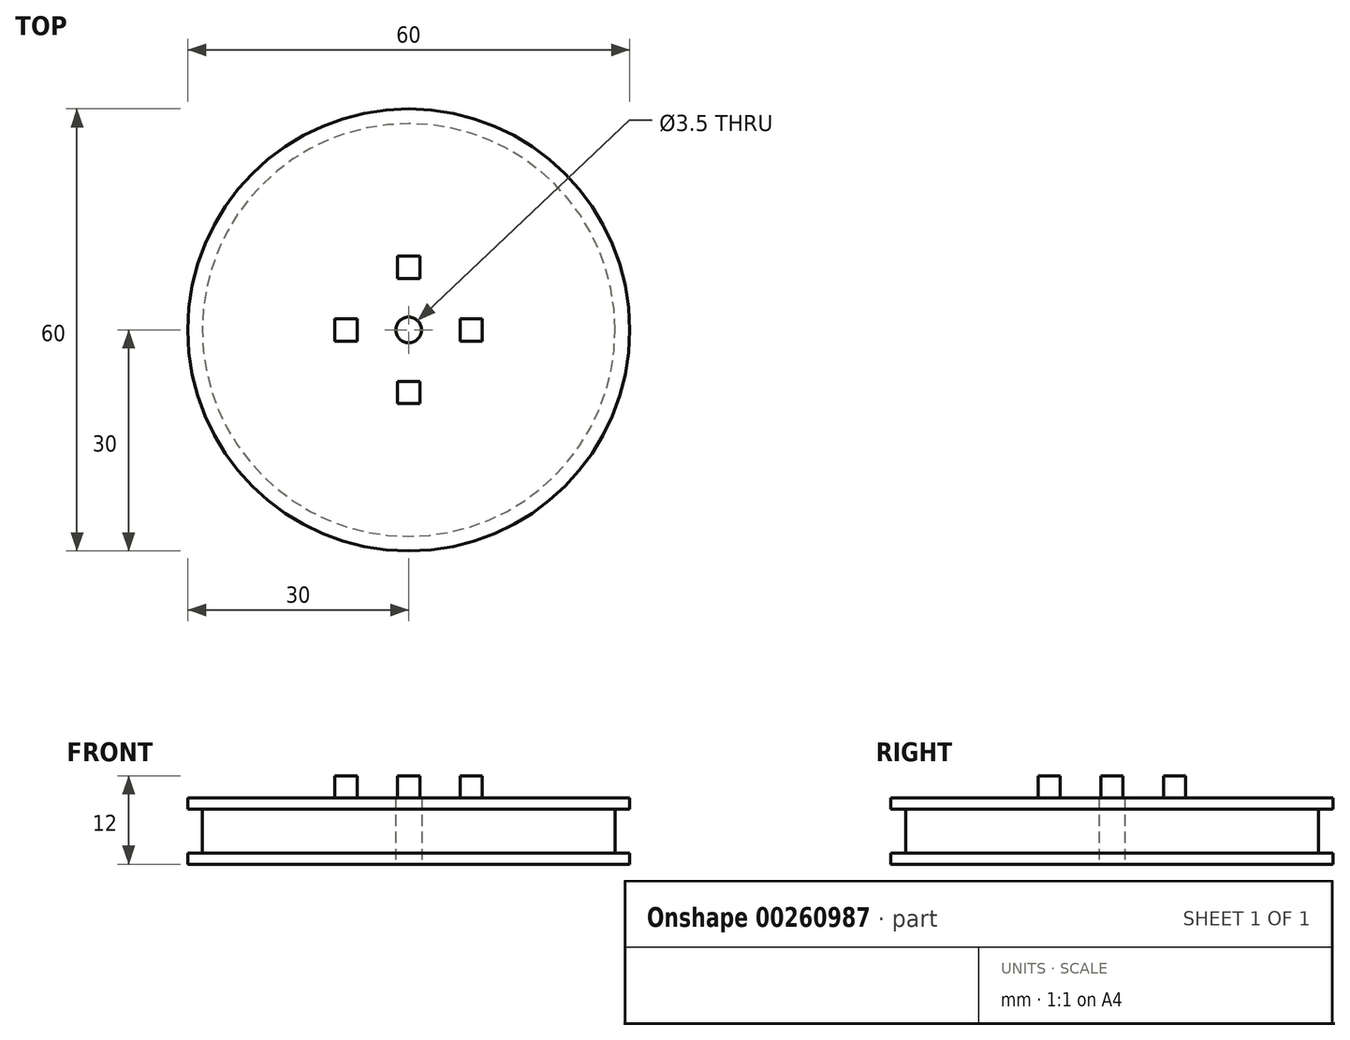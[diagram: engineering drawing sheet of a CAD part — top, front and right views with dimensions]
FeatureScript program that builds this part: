
annotation { "Feature Type Name" : "Feature", "Feature Type Description" : "" }
export const myFeature = defineFeature(function(context is Context, id is Id, definition is map)
    precondition{}
    {
        {
            var Q0;
            Q0=qCreatedBy(makeId("Front.planeOp"),FACE);
            var sketch = newSketch(context, id + "F0", { "sketchPlane" : qUnion([Q0])});
            skLineSegment(sketch, "E0", {"start": v(1.75, 0) * mm, "end": v(27.95, 0) * mm});
            skLineSegment(sketch, "E1", {"start": v(1.75, 0) * mm, "end": v(1.75, 9) * mm});
            skLineSegment(sketch, "E2", {"start": v(0, 0) * mm, "end": v(0, 10) * mm});
            skLineSegment(sketch, "E3", {"start": v(30, 0) * mm, "end": v(30, 1.5) * mm});
            skLineSegment(sketch, "E4", {"start": v(30, 1.5) * mm, "end": v(28, 1.5) * mm});
            skLineSegment(sketch, "E5", {"start": v(27.95, 0) * mm, "end": v(30, 0) * mm});
            skLineSegment(sketch, "E6", {"start": v(28, 1.5) * mm, "end": v(28, 7.5) * mm});
            skLineSegment(sketch, "E7", {"start": v(28, 7.5) * mm, "end": v(30, 7.5) * mm});
            skLineSegment(sketch, "E8", {"start": v(30, 7.5) * mm, "end": v(30, 9) * mm});
            skLineSegment(sketch, "E9", {"start": v(30, 9) * mm, "end": v(1.75, 9) * mm});
            skSolve(sketch);
        }
        {
            var Q0;
            Q0=makeQuery(id+"F0.imprint","IMPRINT",FACE,{"disambiguationData":[TD([[makeQuery(id+"F0.imprint","IMPRINT",EDGE,{"derivedFrom":sQuery(id+"F0.wireOp",EDGE,"E0")}),1.0]])]});
            var Q1;
            Q1=sQuery(id+"F0.wireOp",EDGE,"E2");
            revolve(context, id + "F1", {"entities" : qUnion([Q0]), "axis" : qUnion([Q1]), "revolveType" : RevolveType.FULL});
        }
        {
            var Q0;
            Q0=makeQuery(id+"F1.opRevolve","SWEPT_FACE",FACE,{"disambiguationData":[OSD([sQuery(id+"F0.wireOp",EDGE,"E9")])]});
            var sketch = newSketch(context, id + "F2", { "sketchPlane" : qUnion([Q0])});
            skPoint(sketch, "E10.center", {"position": v(0, 0) * mm});
            skCircle(sketch, "E11", {"center": v(0, 0) * mm, "radius": 15 * mm});
            skLineSegment(sketch, "E12", {"start": v(10, 0) * mm, "end": v(10, 1.5) * mm});
            skLineSegment(sketch, "E13", {"start": v(10, 1.5) * mm, "end": v(7, 1.5) * mm});
            skLineSegment(sketch, "E14", {"start": v(7, 1.5) * mm, "end": v(7, -1.5) * mm});
            skLineSegment(sketch, "E15", {"start": v(7, -1.5) * mm, "end": v(10, -1.5) * mm});
            skLineSegment(sketch, "E16", {"start": v(10, -1.5) * mm, "end": v(10, 0) * mm});
            skLineSegment(sketch, "E17.1.0", {"start": v(-1.5, -7) * mm, "end": v(-1.5, -10) * mm});
            skLineSegment(sketch, "E17.1.1", {"start": v(0, -10) * mm, "end": v(1.5, -10) * mm});
            skLineSegment(sketch, "E17.1.2", {"start": v(1.5, -7) * mm, "end": v(-1.5, -7) * mm});
            skLineSegment(sketch, "E17.1.3", {"start": v(-1.5, -10) * mm, "end": v(0, -10) * mm});
            skLineSegment(sketch, "E17.1.4", {"start": v(1.5, -10) * mm, "end": v(1.5, -7) * mm});
            skLineSegment(sketch, "E17.2.0", {"start": v(-7, 1.5) * mm, "end": v(-10, 1.5) * mm});
            skLineSegment(sketch, "E17.2.1", {"start": v(-10, 0) * mm, "end": v(-10, -1.5) * mm});
            skLineSegment(sketch, "E17.2.2", {"start": v(-7, -1.5) * mm, "end": v(-7, 1.5) * mm});
            skLineSegment(sketch, "E17.2.3", {"start": v(-10, 1.5) * mm, "end": v(-10, 0) * mm});
            skLineSegment(sketch, "E17.2.4", {"start": v(-10, -1.5) * mm, "end": v(-7, -1.5) * mm});
            skLineSegment(sketch, "E17.anchor1", {"start": v(0, 0) * mm, "end": v(7, -1.5) * mm, "construction": true});
            skLineSegment(sketch, "E17.anchor2", {"start": v(0, 0) * mm, "end": v(-7, 1.5) * mm, "construction": true});
            skLineSegment(sketch, "E18", {"start": v(0, 0) * mm, "end": v(-0.46, 0) * mm});
            skLineSegment(sketch, "E19.MirrorCS", {"start": v(1.5, 7) * mm, "end": v(-1.5, 7) * mm});
            skLineSegment(sketch, "E20.MirrorCS", {"start": v(0, 10) * mm, "end": v(1.5, 10) * mm});
            skLineSegment(sketch, "E21.MirrorCS", {"start": v(-1.5, 7) * mm, "end": v(-1.5, 10) * mm});
            skLineSegment(sketch, "E22.MirrorCS", {"start": v(-1.5, 10) * mm, "end": v(0, 10) * mm});
            skLineSegment(sketch, "E23.MirrorCS", {"start": v(1.5, 10) * mm, "end": v(1.5, 7) * mm});
            skSolve(sketch);
        }
        {
            var Q0;
            Q0=makeQuery(id+"F2.imprint","IMPRINT",FACE,{"disambiguationData":[TD([[makeQuery(id+"F2.imprint","IMPRINT",EDGE,{"derivedFrom":sQuery(id+"F2.wireOp",EDGE,"E19.MirrorCS")}),-1.0]])]});
            var Q1;
            Q1=makeQuery(id+"F2.imprint","IMPRINT",FACE,{"disambiguationData":[TD([[makeQuery(id+"F2.imprint","IMPRINT",EDGE,{"derivedFrom":sQuery(id+"F2.wireOp",EDGE,"E17.1.0")}),1.0]])]});
            var Q2;
            Q2=makeQuery(id+"F2.imprint","IMPRINT",FACE,{"disambiguationData":[TD([[makeQuery(id+"F2.imprint","IMPRINT",EDGE,{"derivedFrom":sQuery(id+"F2.wireOp",EDGE,"E17.2.0")}),1.0]])]});
            var Q3;
            Q3=makeQuery(id+"F2.imprint","IMPRINT",FACE,{"disambiguationData":[TD([[makeQuery(id+"F2.imprint","IMPRINT",EDGE,{"derivedFrom":sQuery(id+"F2.wireOp",EDGE,"E12")}),1.0]])]});
            extrude(context, id + "F3", {"entities" : qUnion([Q0, Q1, Q2, Q3]), "operationType" : NewBodyOperationType.ADD, "depth" : 3 * mm, "offsetDistance" : 25 * mm});
        }
        {
            var Q0;
            Q0=makeQuery(id+"F2.imprint","IMPRINT",FACE,{"disambiguationData":[TD([[makeQuery(id+"F2.imprint","IMPRINT",EDGE,{"derivedFrom":sQuery(id+"F2.wireOp",EDGE,"E19.MirrorCS")}),-1.0]])]});
            var Q1;
            Q1=makeQuery(id+"F2.imprint","IMPRINT",FACE,{"disambiguationData":[TD([[makeQuery(id+"F2.imprint","IMPRINT",EDGE,{"derivedFrom":sQuery(id+"F2.wireOp",EDGE,"E17.2.0")}),1.0]])]});
            var Q2;
            Q2=makeQuery(id+"F2.imprint","IMPRINT",FACE,{"disambiguationData":[TD([[makeQuery(id+"F2.imprint","IMPRINT",EDGE,{"derivedFrom":sQuery(id+"F2.wireOp",EDGE,"E17.1.0")}),1.0]])]});
            var Q3;
            Q3=makeQuery(id+"F2.imprint","IMPRINT",FACE,{"disambiguationData":[TD([[makeQuery(id+"F2.imprint","IMPRINT",EDGE,{"derivedFrom":sQuery(id+"F2.wireOp",EDGE,"E12")}),1.0]])]});
            extrude(context, id + "F4", {"entities" : qUnion([Q0, Q1, Q2, Q3]), "operationType" : NewBodyOperationType.ADD, "depth" : 3 * mm, "offsetDistance" : 25 * mm});
        }
    });
